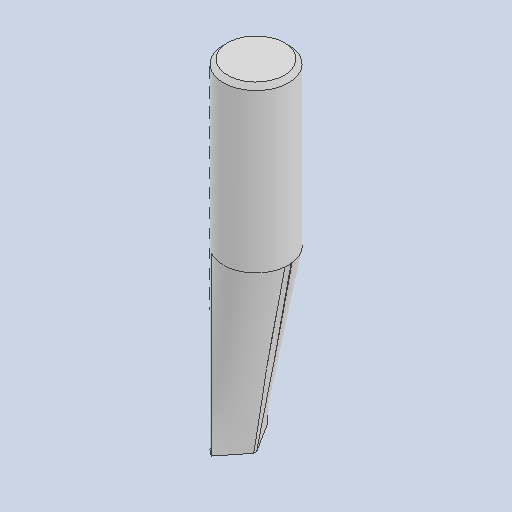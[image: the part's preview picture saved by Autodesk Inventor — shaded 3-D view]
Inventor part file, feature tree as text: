
AUTODESK INVENTOR PART (.ipt)
format: ipt  version: 2024 (Build 280153000, 153)  size: 205,824 bytes
history: native  units: in
note: dims shown in document units (in); Inventor stores cm internally (conversion verified against a paired STEP export)
features: chamfer x1
ambient origin geometry x8: Origin, YZ Plane, XZ Plane, XY Plane, X Axis, Y Axis, Z Axis, Center Point
bodies: Solid1 (feature_tree)
feature tree (1):
  chamfer  "Chamfer1"  [1 undecoded]
note: 1 required parameter value undecoded (feature->parameter linkage not recoverable at this tier; creation-order binding heuristic only, values carry confidence <= 0.55)
